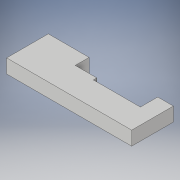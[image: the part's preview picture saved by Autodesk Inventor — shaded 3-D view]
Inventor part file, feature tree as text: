
AUTODESK INVENTOR PART (.ipt)
format: ipt  version: 2018.2 (Build 222227000, 227)  size: 101,376 bytes
history: native  units: in
note: dims shown in document units (in); Inventor stores cm internally (conversion verified against a paired STEP export)
features: extrude x1, sketch x1
ambient origin geometry x8: Origin, YZ Plane, XZ Plane, XY Plane, X Axis, Y Axis, Z Axis, Center Point
bodies: Solid1 (feature_tree)
feature tree (2):
  extrude  "Extrusion1"  Depth=3.0in
  sketch  "Sketch1"  dims[d0=9.0in d2=3.0in d3=1.125in d4=1.25in d5=3.375in d6=0.25in d7=1.5625in d9=1.0in d10=0.0in]
